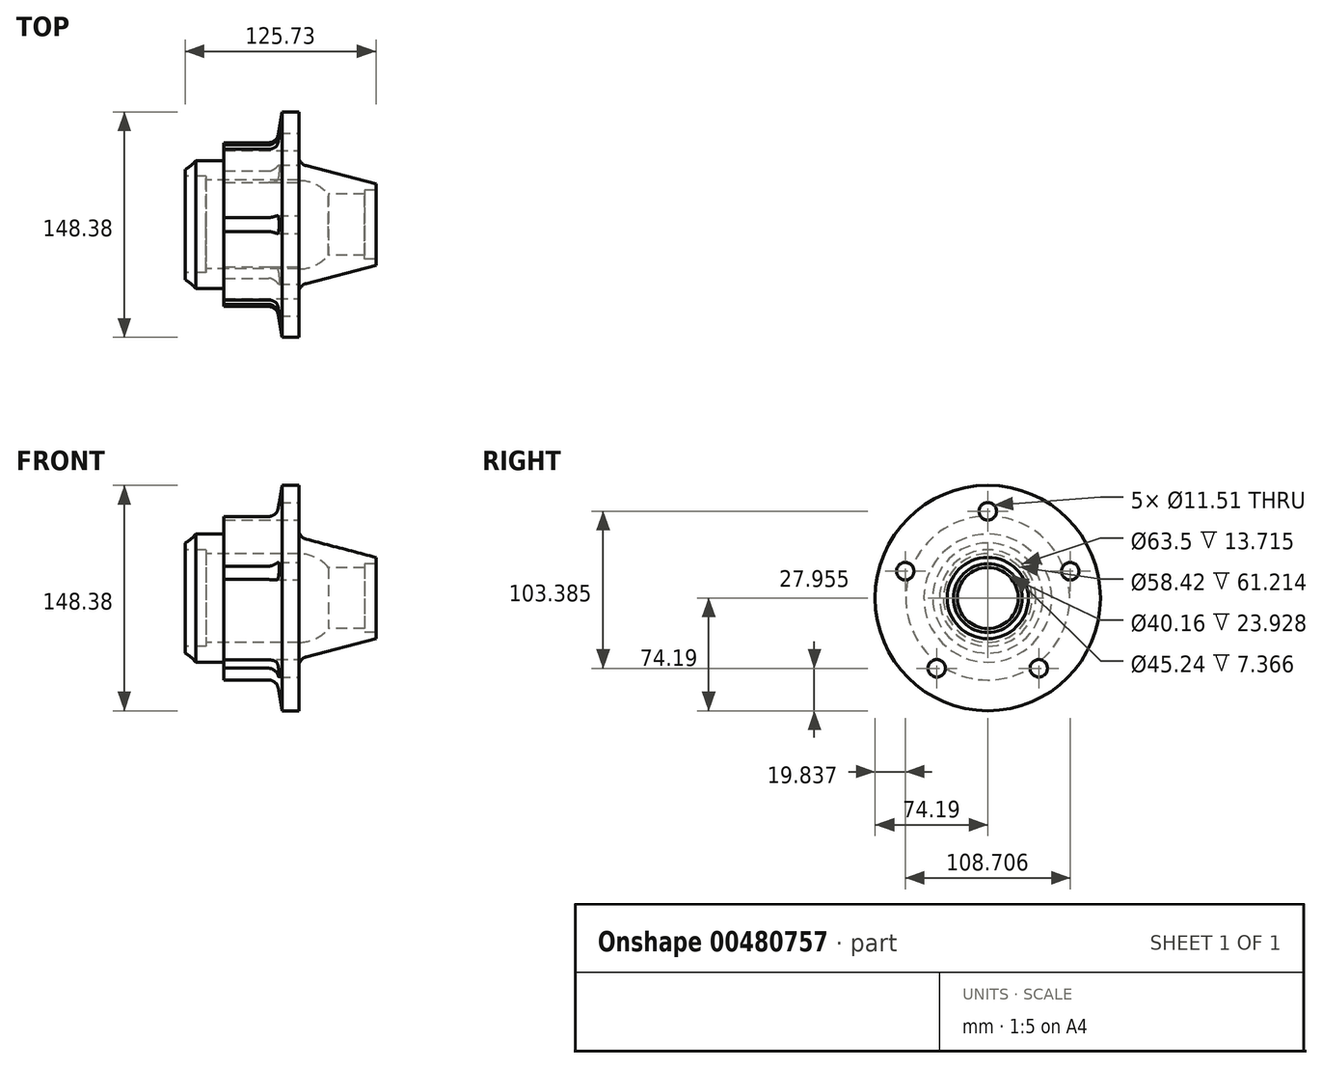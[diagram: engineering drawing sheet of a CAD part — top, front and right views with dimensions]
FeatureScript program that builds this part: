
annotation { "Feature Type Name" : "Feature", "Feature Type Description" : "" }
export const myFeature = defineFeature(function(context is Context, id is Id, definition is map)
    precondition{}
    {
        {
            var Q0;
            Q0=qCreatedBy(makeId("Front.planeOp"),FACE);
            var sketch = newSketch(context, id + "F0", { "sketchPlane" : qUnion([Q0])});
            skLineSegment(sketch, "E0", {"start": v(0, 0) * mm, "end": v(157.88, 0) * mm, "construction": true});
            skLineSegment(sketch, "E1", {"start": v(0, 44.95) * mm, "end": v(0, 74.2) * mm});
            skLineSegment(sketch, "E2", {"start": v(0, 74.2) * mm, "end": v(-10.89, 74.2) * mm});
            skLineSegment(sketch, "E3", {"start": v(-10.89, 74.2) * mm, "end": v(-14.6, 53.93) * mm});
            skLineSegment(sketch, "E4", {"start": v(-14.6, 53.93) * mm, "end": v(-49.28, 53.93) * mm});
            skLineSegment(sketch, "E5", {"start": v(-49.28, 53.93) * mm, "end": v(-49.28, 42.1) * mm});
            skLineSegment(sketch, "E6", {"start": v(-49.28, 42.1) * mm, "end": v(-67.95, 42.1) * mm});
            skArc(sketch, "E7", {"start": v(-74.93, 36.26) * mm, "mid": v(-71.12, 38.81) * mm, "end": v(-67.95, 42.1) * mm});
            skLineSegment(sketch, "E8", {"start": v(-74.93, 36.26) * mm, "end": v(-74.93, 31.75) * mm});
            skLineSegment(sketch, "E9", {"start": v(-74.93, 31.75) * mm, "end": v(-61.21, 31.75) * mm});
            skLineSegment(sketch, "E10", {"start": v(-61.21, 31.75) * mm, "end": v(-61.21, 29.2) * mm});
            skLineSegment(sketch, "E11", {"start": v(-61.21, 29.2) * mm, "end": v(0, 29.2) * mm});
            skArc(sketch, "E12", {"start": v(0, 29.2) * mm, "mid": v(10.77, 26.81) * mm, "end": v(19.5, 20.08) * mm});
            skArc(sketch, "E13", {"start": v(0, 44.95) * mm, "mid": v(1.32, 41.07) * mm, "end": v(4.74, 38.8) * mm});
            skLineSegment(sketch, "E14", {"start": v(4.74, 38.8) * mm, "end": v(50.8, 26.75) * mm});
            skLineSegment(sketch, "E15", {"start": v(50.8, 26.75) * mm, "end": v(50.8, 22.62) * mm});
            skLineSegment(sketch, "E16", {"start": v(50.8, 22.62) * mm, "end": v(43.43, 22.62) * mm});
            skLineSegment(sketch, "E17", {"start": v(43.43, 22.62) * mm, "end": v(43.43, 20.08) * mm});
            skLineSegment(sketch, "E18", {"start": v(43.43, 20.08) * mm, "end": v(19.5, 20.08) * mm});
            skLineSegment(sketch, "E19", {"start": v(0, 57.15) * mm, "end": v(-14, 57.15) * mm, "construction": true});
            skLineSegment(sketch, "E20", {"start": v(-49.28, 49.21) * mm, "end": v(-37.58, 49.21) * mm, "construction": true});
            skSolve(sketch);
        }
        {
            var Q0;
            Q0=qSketchRegion(id+"F0",true);
            var Q1;
            Q1=sQuery(id+"F0.wireOp",EDGE,"E0");
            revolve(context, id + "F1", {"entities" : qUnion([Q0]), "axis" : qUnion([Q1]), "revolveType" : RevolveType.FULL});
        }
        {
            var Q0;
            Q0=qCreatedBy(makeId("Right.planeOp"),FACE);
            var sketch = newSketch(context, id + "F2", { "sketchPlane" : qUnion([Q0])});
            skPoint(sketch, "E21", {"position": v(0, 57.15) * mm});
            skPoint(sketch, "E22.1.0", {"position": v(-54.35, 17.66) * mm});
            skPoint(sketch, "E22.2.0", {"position": v(-33.6, -46.24) * mm});
            skPoint(sketch, "E22.3.0", {"position": v(33.6, -46.24) * mm});
            skPoint(sketch, "E22.4.0", {"position": v(54.35, 17.66) * mm});
            skPoint(sketch, "E22.center", {"position": v(0, 0) * mm});
            skSolve(sketch);
        }
        {
            var Q0;
            Q0=sQuery(id+"F2.wireOp",VERTEX,"E21");
            var Q1;
            Q1=sQuery(id+"F2.wireOp",VERTEX,"E22.4.0");
            var Q2;
            Q2=sQuery(id+"F2.wireOp",VERTEX,"E22.3.0");
            var Q3;
            Q3=sQuery(id+"F2.wireOp",VERTEX,"E22.2.0");
            var Q4;
            Q4=sQuery(id+"F2.wireOp",VERTEX,"E22.1.0");
            var Q5;
            Q5=makeQuery(id+"F1.opRevolve","SWEPT_BODY",BODY,{"disambiguationData":[OSD([sQuery(id+"F0.wireOp",EDGE,"E1"),sQuery(id+"F0.wireOp",EDGE,"E2"),sQuery(id+"F0.wireOp",EDGE,"E3"),sQuery(id+"F0.wireOp",EDGE,"E4"),sQuery(id+"F0.wireOp",EDGE,"E5"),sQuery(id+"F0.wireOp",EDGE,"E6"),sQuery(id+"F0.wireOp",EDGE,"E7"),sQuery(id+"F0.wireOp",EDGE,"E8"),sQuery(id+"F0.wireOp",EDGE,"E9"),sQuery(id+"F0.wireOp",EDGE,"E10"),sQuery(id+"F0.wireOp",EDGE,"E11"),sQuery(id+"F0.wireOp",EDGE,"E12"),sQuery(id+"F0.wireOp",EDGE,"E13"),sQuery(id+"F0.wireOp",EDGE,"E14"),sQuery(id+"F0.wireOp",EDGE,"E15"),sQuery(id+"F0.wireOp",EDGE,"E16"),sQuery(id+"F0.wireOp",EDGE,"E17"),sQuery(id+"F0.wireOp",EDGE,"E18")])]});
            hole(context, id + "F3", {"style" : HoleStyle.SIMPLE, "endStyle" : HoleEndStyle.THROUGH, "standardTappedOrClearance" : lookupTablePath({ "standard" : "ANSI", "engagement" : "75%", "pitch" : "20 tpi", "size" : "1/2", "type" : "Tapped" }), "standardBlindInLast" : lookupTablePath({ "standard" : "ANSI", "engagement" : "75%", "pitch" : "20 tpi", "size" : "1/2", "type" : "Tapped" }), "holeDiameter" : 11.5 * mm, "showTappedDepth" : true, "isTappedThrough" : true, "tappedDepth" : 12.7 * mm, "tapClearance" : 3, "locations" : qUnion([Q0, Q1, Q2, Q3, Q4]), "scope" : qUnion([Q5]), "majorDiameter" : 12.7 * mm});
        }
        {
            var Q0;
            Q0=makeQuery(id+"F1.opRevolve","SWEPT_EDGE",EDGE,{"disambiguationData":[OSD([sQuery(id+"F0.wireOp",EDGE,"E3"),sQuery(id+"F0.wireOp",EDGE,"E4")])]});
            fillet(context, id + "F4", {"entities" : qUnion([Q0]), "radius" : 6.35 * mm, "tangentPropagation" : true, "allowEdgeOverflow" : false});
        }
    });
